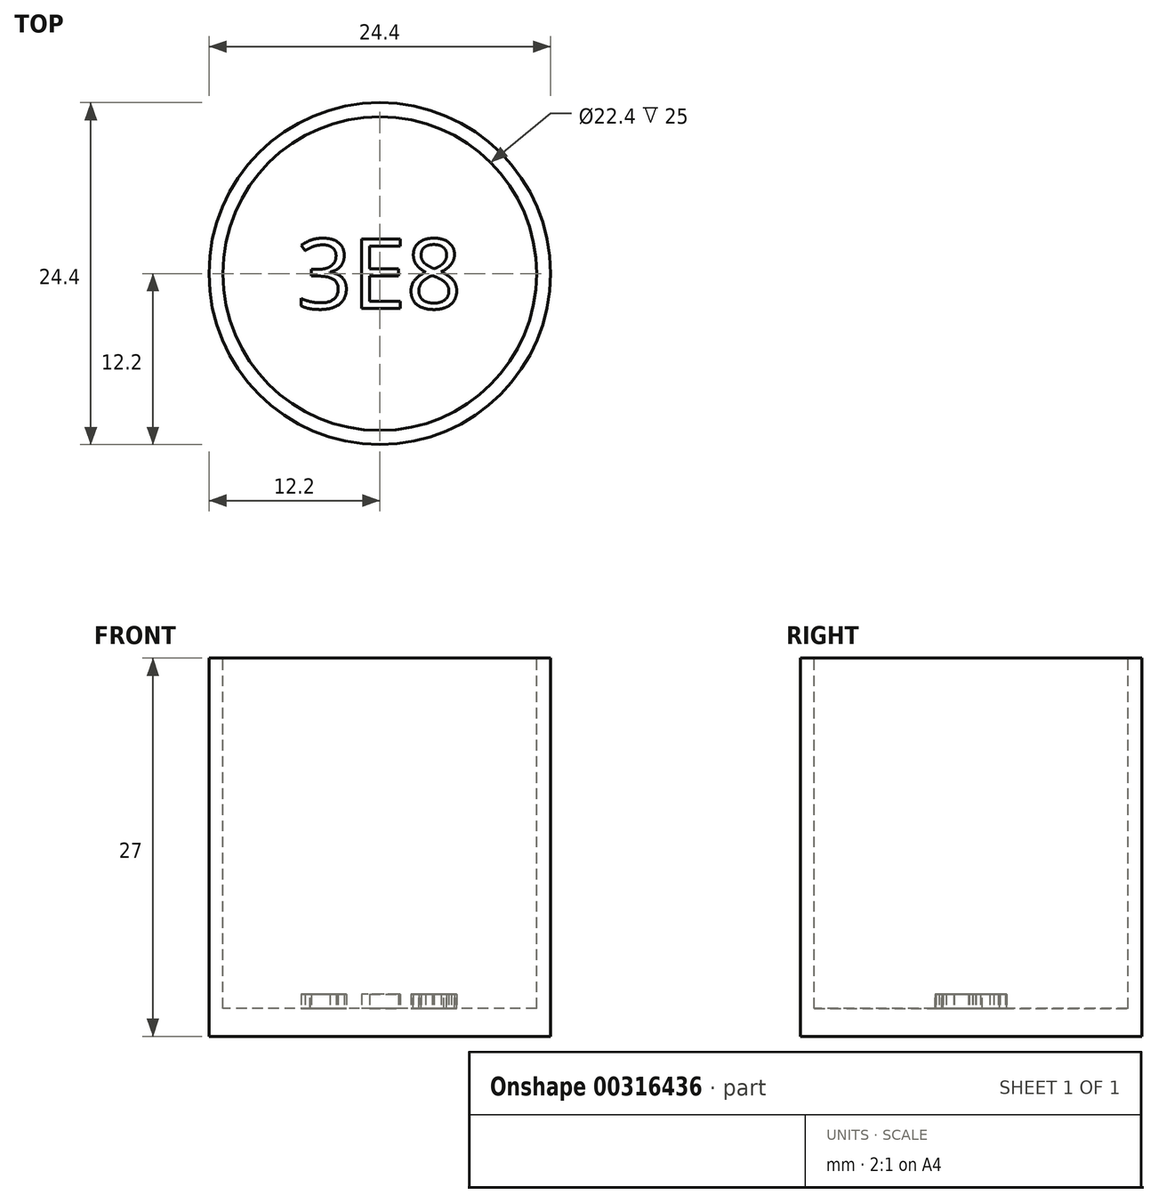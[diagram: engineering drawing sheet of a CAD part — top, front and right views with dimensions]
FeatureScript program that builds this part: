
annotation { "Feature Type Name" : "Feature", "Feature Type Description" : "" }
export const myFeature = defineFeature(function(context is Context, id is Id, definition is map)
    precondition{}
    {
        {
            assignVariable(context, id + "F0", {"name" : "length", "anyValue" : 25});
        }
        {
            assignVariable(context, id + "F1", {"name" : "wallthick", "anyValue" : 2});
        }
        {
            var Q0;
            Q0=qCreatedBy(makeId("Top.planeOp"),FACE);
            var sketch = newSketch(context, id + "F2", { "sketchPlane" : qUnion([Q0])});
            skCircle(sketch, "E0", {"center": v(0, 0) * mm, "radius": 12.2 * mm});
            skSolve(sketch);
        }
        {
            var Q0;
            Q0 = qSketchRegion(id + "F2", true);
            extrude(context, id + "F3", {"entities" : qUnion([Q0]), "depth" : (getVariable(context, 'length') + getVariable(context, 'wallthick')) * mm});
        }
        {
            var Q0;
            Q0=makeQuery(id+"F3.opExtrude","CAP_FACE",FACE,{"disambiguationData":[OSD([sQuery(id+"F2.wireOp",EDGE,"E0")])],"isStart":false});
            var sketch = newSketch(context, id + "F4", { "sketchPlane" : qUnion([Q0])});
            skCircle(sketch, "E1", {"center": v(0, 0) * mm, "radius": 11.2 * mm});
            skSolve(sketch);
        }
        {
            var Q0;
            Q0 = qSketchRegion(id + "F4", true);
            extrude(context, id + "F5", {"entities" : qUnion([Q0]), "operationType" : NewBodyOperationType.REMOVE, "oppositeDirection" : true, "depth" : (getVariable(context, 'length')) * mm});
        }
        {
            var Q0;
            Q0=makeQuery(id+"F5.boolean.opBoolean","COPY",FACE,{"derivedFrom":makeQuery(id+"F5.opExtrude","CAP_FACE",FACE,{"disambiguationData":[OSD([sQuery(id+"F4.wireOp",EDGE,"E1")])],"isStart":false})});
            var sketch = newSketch(context, id + "F6", { "sketchPlane" : qUnion([Q0])});
            skText(sketch, "E2", { "text": "3E8", "fontName": "OpenSans-Regular.ttf"});
            const initialGuessF6  = {"E2": [-0.00595, -0.0025, 1, 0, 0.005]};
            skSetInitialGuess(sketch, initialGuessF6);
            skSolve(sketch);
        }
        {
            var Q0;
            Q0 = qSketchRegion(id + "F6", true);
            extrude(context, id + "F7", {"entities" : qUnion([Q0]), "operationType" : NewBodyOperationType.ADD, "depth" : 1 * mm});
        }
    });
